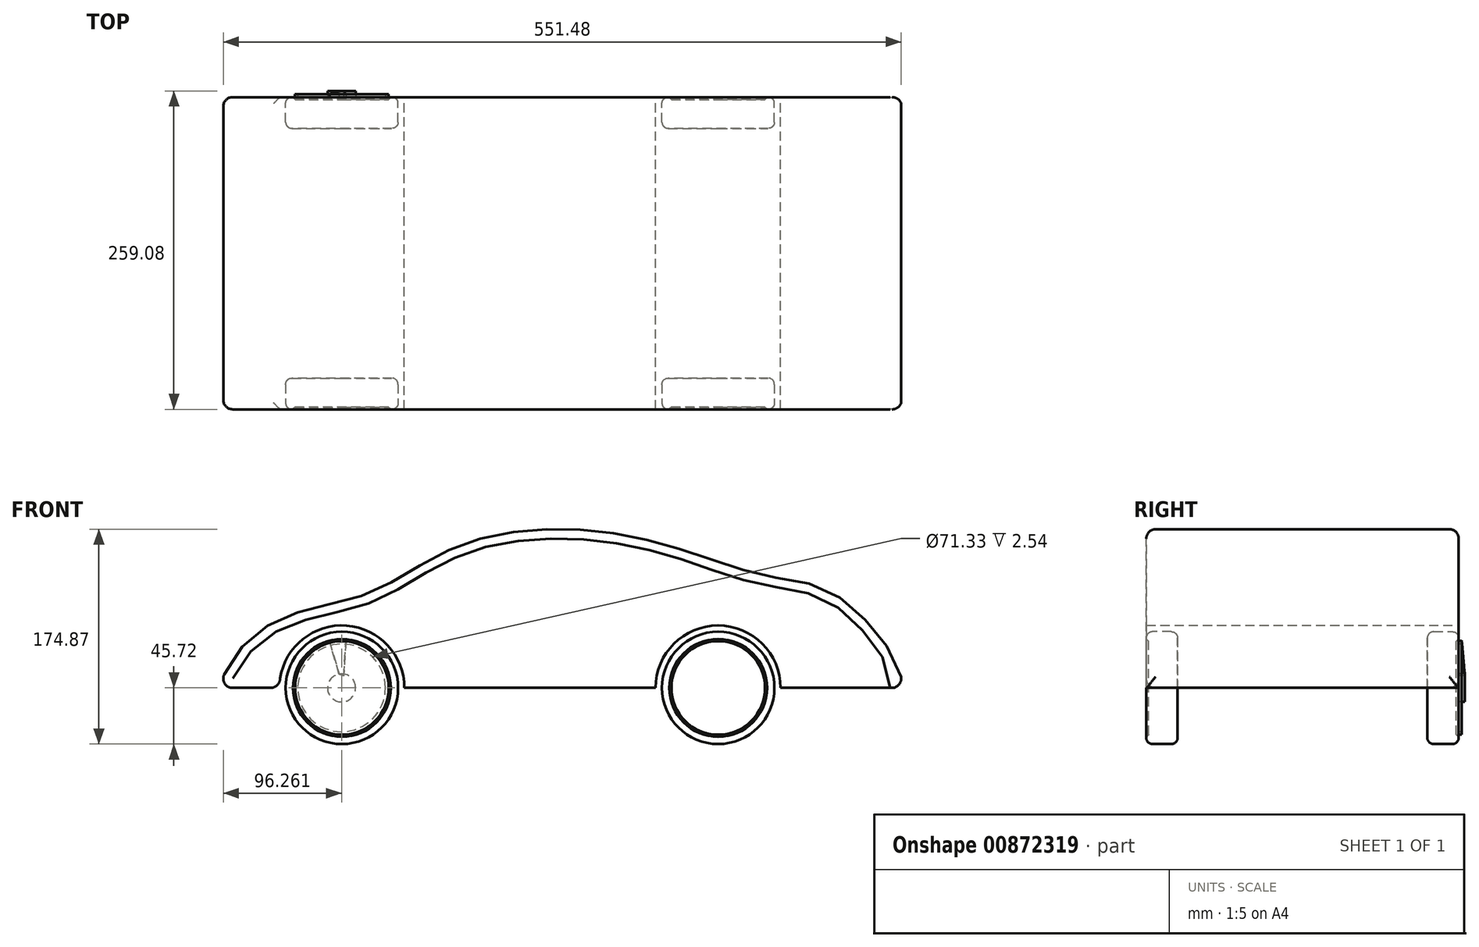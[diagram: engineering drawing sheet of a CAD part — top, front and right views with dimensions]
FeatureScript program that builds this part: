
annotation { "Feature Type Name" : "Feature", "Feature Type Description" : "" }
export const myFeature = defineFeature(function(context is Context, id is Id, definition is map)
    precondition{}
    {
        {
            var Q0;
            Q0=qCreatedBy(makeId("Front.planeOp"),FACE);
            var sketch = newSketch(context, id + "F0", { "sketchPlane" : qUnion([Q0])});
            skFitSpline(sketch, "E0", {"points": [v(0, 0) * mm, v(73.7, 64) * mm, v(127.71, 79.17) * mm, v(203.51, 118.59) * mm, v(340.8, 122.3) * mm, v(442.02, 91.83) * mm, v(507.62, 71.94) * mm, v(554.71, 0) * mm], "startDerivative": vector(332.9, 896.63) * mm, "endDerivative": vector(-140, -298.92) * mm});
            skLineSegment(sketch, "E1", {"start": v(0, 0) * mm, "end": v(49.58, 0) * mm});
            skCircle(sketch, "E2", {"center": v(100.38, 0) * mm, "radius": 50.8 * mm});
            skCircle(sketch, "E3", {"center": v(406.34, 0) * mm, "radius": 50.8 * mm});
            skLineSegment(sketch, "E4.trimOffspring", {"start": v(151.18, 0) * mm, "end": v(355.54, 0) * mm});
            skLineSegment(sketch, "E5.trimOffspring", {"start": v(457.14, 0) * mm, "end": v(554.71, 0) * mm});
            skPoint(sketch, "E6", {"position": v(253.36, 0) * mm});
            skSolve(sketch);
        }
        {
            var Q0;
            Q0=makeQuery(id+"F0.imprint","IMPRINT",FACE,{"disambiguationData":[TD([[makeQuery(id+"F0.imprint","IMPRINT",EDGE,{"derivedFrom":sQuery(id+"F0.wireOp",EDGE,"E0")}),-1.0]])]});
            extrude(context, id + "F1", {"entities" : qUnion([Q0]), "depth" : 254 * mm, "offsetDistance" : 25.4 * mm});
        }
        {
            var Q0;
            Q0=qCreatedBy(makeId("Front.planeOp"),FACE);
            var sketch = newSketch(context, id + "F2", { "sketchPlane" : qUnion([Q0])});
            skCircle(sketch, "E7", {"center": v(100.38, 0) * mm, "radius": 45.72 * mm});
            skSolve(sketch);
        }
        {
            var Q0;
            Q0 = qSketchRegion(id + "F2", true);
            extrude(context, id + "F3", {"entities" : qUnion([Q0]), "depth" : 25.4 * mm, "offsetDistance" : 25.4 * mm});
        }
        {
            var Q0;
            Q0=makeQuery(id+"F1.opExtrude","SWEPT_FACE",FACE,{"disambiguationData":[OSD([sQuery(id+"F0.wireOp",EDGE,"E1")])]});
            var Q1;
            Q1=makeQuery(id+"F1.opExtrude","SWEPT_FACE",FACE,{"disambiguationData":[OSD([sQuery(id+"F0.wireOp",EDGE,"E0")])]});
            fillet(context, id + "F4", {"entities" : qUnion([Q0, Q1]), "radius" : 7.62 * mm, "tangentPropagation" : true, "allowEdgeOverflow" : false});
        }
        {
            var Q0;
            Q0=makeQuery(id+"F3.opExtrude","CAP_FACE",FACE,{"disambiguationData":[OSD([sQuery(id+"F2.wireOp",EDGE,"E7")])],"isStart":true});
            var Q1;
            Q1=makeQuery(id+"F3.opExtrude","SWEPT_FACE",FACE,{"disambiguationData":[OSD([sQuery(id+"F2.wireOp",EDGE,"E7")])]});
            fillet(context, id + "F5", {"entities" : qUnion([Q0, Q1]), "radius" : 5.08 * mm, "tangentPropagation" : true, "allowEdgeOverflow" : false});
        }
        {
            var Q0;
            Q0=makeQuery(id+"F3.opExtrude","CAP_FACE",FACE,{"disambiguationData":[OSD([sQuery(id+"F2.wireOp",EDGE,"E7")])],"isStart":true});
            extrude(context, id + "F6", {"entities" : qUnion([Q0]), "operationType" : NewBodyOperationType.REMOVE, "oppositeDirection" : true, "depth" : 1.9 * mm, "offsetDistance" : 25.4 * mm, "hasDraft" : true, "draftAngle" : 3 * degree});
        }
        {
            var Q0;
            Q0=makeQuery(id+"F6.boolean.opBoolean","COPY",EDGE,{"derivedFrom":makeQuery(id+"F6.opExtrude","CAP_EDGE",EDGE,{"disambiguationData":[OSD([sQuery(id+"F2.wireOp",EDGE,"E7")])],"isStart":false})});
            chamfer(context, id + "F7", {"entities" : qUnion([Q0]), "width" : 2.54 * mm, "tangentPropagation" : true});
        }
        {
            var Q0;
            Q0=makeQuery(id+"F3.opExtrude","SWEPT_BODY",BODY,{"disambiguationData":[OSD([sQuery(id+"F2.wireOp",EDGE,"E7")])]});
            var Q1;
            Q1=qCreatedBy(makeId("Front.planeOp"),FACE);
            mirror(context, id + "F8", {"entities" : qUnion([Q0]), "mirrorPlane" : qUnion([Q1])});
        }
        {
            var Q0;
            Q0=makeQuery(id+"F8.opPattern","COPY",BODY,{"derivedFrom":makeQuery(id+"F3.opExtrude","SWEPT_BODY",BODY,{"disambiguationData":[OSD([sQuery(id+"F2.wireOp",EDGE,"E7")])]}),"instanceName":"1"});
            transform(context, id + "F9", {"entities" : qUnion([Q0]), "transformType" : TransformType.TRANSLATION_3D, "dx" : 0 * mm, "dy" : -254 * mm, "dz" : 0 * mm, "makeCopy" : false});
        }
        {
            var Q0;
            Q0=makeQuery(id+"F8.opPattern","COPY",BODY,{"derivedFrom":makeQuery(id+"F9.opPattern","COPY",BODY,{"derivedFrom":makeQuery(id+"F3.opExtrude","SWEPT_BODY",BODY,{"disambiguationData":[OSD([sQuery(id+"F2.wireOp",EDGE,"E7")])]}),"instanceName":"1"}),"instanceName":"1"});
            var Q1;
            Q1=makeQuery(id+"F3.opExtrude","SWEPT_BODY",BODY,{"disambiguationData":[OSD([sQuery(id+"F2.wireOp",EDGE,"E7")])]});
            var Q2;
            Q2=makeQuery(id+"F8.opPattern","COPY",BODY,{"derivedFrom":makeQuery(id+"F3.opExtrude","SWEPT_BODY",BODY,{"disambiguationData":[OSD([sQuery(id+"F2.wireOp",EDGE,"E7")])]}),"instanceName":"1"});
            transform(context, id + "F10", {"entities" : qUnion([Q0, Q1, Q2]), "transformType" : TransformType.TRANSLATION_3D, "dx" : 306.07 * mm, "dy" : 0 * mm, "dz" : 0 * mm, "makeCopy" : true});
        }
        {
            var Q0;
            Q0=makeQuery(id+"F2.imprint","IMPRINT",FACE,{"disambiguationData":[TD([[makeQuery(id+"F2.imprint","IMPRINT",EDGE,{"derivedFrom":sQuery(id+"F2.wireOp",EDGE,"E7")}),1.0]])]});
            var sketch = newSketch(context, id + "F11", { "sketchPlane" : qUnion([Q0])});
            skCircle(sketch, "E8", {"center": v(100.14, 0) * mm, "radius": 38.1 * mm});
            skCircle(sketch, "E9", {"center": v(100.14, 0) * mm, "radius": 35.66 * mm});
            skCircle(sketch, "E10", {"center": v(100.14, 0) * mm, "radius": 11.43 * mm});
            skSolve(sketch);
        }
        {
            var Q0;
            Q0=makeQuery(id+"F11.imprint","IMPRINT",FACE,{"disambiguationData":[TD([[makeQuery(id+"F11.imprint","IMPRINT",EDGE,{"derivedFrom":sQuery(id+"F11.wireOp",EDGE,"E10")}),1.0]])]});
            var Q1;
            Q1=makeQuery(id+"F11.imprint","IMPRINT",FACE,{"disambiguationData":[TD([[makeQuery(id+"F11.imprint","IMPRINT",EDGE,{"derivedFrom":sQuery(id+"F11.wireOp",EDGE,"E8")}),1.0]])]});
            extrude(context, id + "F12", {"entities" : qUnion([Q0, Q1]), "oppositeDirection" : true, "depth" : 2.54 * mm, "offsetDistance" : 25.4 * mm});
        }
        {
            var Q0;
            Q0=makeQuery(id+"F12.opExtrude","CAP_FACE",FACE,{"disambiguationData":[OSD([sQuery(id+"F11.wireOp",EDGE,"E10")])],"isStart":false});
            extrude(context, id + "F13", {"entities" : qUnion([Q0]), "operationType" : NewBodyOperationType.ADD, "depth" : 2.54 * mm, "offsetDistance" : 25.4 * mm});
        }
        {
            var Q0;
            Q0=makeQuery(id+"F12.opExtrude","CAP_FACE",FACE,{"disambiguationData":[OSD([sQuery(id+"F11.wireOp",EDGE,"E8"),sQuery(id+"F11.wireOp",EDGE,"E9")])],"isStart":false});
            var sketch = newSketch(context, id + "F14", { "sketchPlane" : qUnion([Q0])});
            skLineSegment(sketch, "E11", {"start": v(-138.24, 0) * mm, "end": v(0, 0) * mm, "construction": true});
            skLineSegment(sketch, "E12", {"start": v(-99.53, -38.1) * mm, "end": v(-99.53, 54.44) * mm, "construction": true});
            skPoint(sketch, "E13", {"position": v(-99.53, 9.67) * mm});
            skLineSegment(sketch, "E14", {"start": v(-101.9, 9.63) * mm, "end": v(-103.6, 37.64) * mm});
            skLineSegment(sketch, "E15", {"start": v(-95.99, 37.64) * mm, "end": v(-97.7, 9.63) * mm});
            skLineSegment(sketch, "E16", {"start": v(-103.6, 37.64) * mm, "end": v(-95.99, 37.64) * mm});
            skLineSegment(sketch, "E17", {"start": v(-101.9, 9.63) * mm, "end": v(-97.7, 9.63) * mm});
            skSolve(sketch);
        }
        {
            var Q0;
            {var subQ0=sQuery(id+"F14.wireOp",EDGE,"E17");Q0=makeQuery(id+"F14.imprint","IMPRINT",FACE,{"disambiguationData":[TD([[makeQuery(id+"F14.imprint","IMPRINT",EDGE,{"derivedFrom":subQ0}),1.0]])]});}
            var Q1;
            {var subQ0=sQuery(id+"F14.wireOp",EDGE,"E16");Q1=makeQuery(id+"F14.imprint","IMPRINT",FACE,{"disambiguationData":[TD([[makeQuery(id+"F14.imprint","IMPRINT",EDGE,{"derivedFrom":subQ0}),-1.0]])]});}
            var Q2;
            Q2=sQuery(id+"F14.wireOp",EDGE,"E17");
            var Q3;
            Q3=sQuery(id+"F14.wireOp",EDGE,"E15");
            var Q4;
            Q4=sQuery(id+"F14.wireOp",EDGE,"E16");
            var Q5;
            Q5=sQuery(id+"F14.wireOp",EDGE,"E14");
            extrude(context, id + "F15", {"entities" : qUnion([Q0, Q1]), "surfaceEntities" : qUnion([Q2, Q3, Q4, Q5]), "depth" : 5.08 * mm, "offsetDistance" : 25.4 * mm});
        }
        {
            var Q0;
            Q0=makeQuery(id+"F15.opExtrude","SWEPT_FACE",FACE,{"disambiguationData":[OSD([sQuery(id+"F14.wireOp",EDGE,"E14")])]});
            var sketch = newSketch(context, id + "F16", { "sketchPlane" : qUnion([Q0])});
            skLineSegment(sketch, "E18", {"start": v(5.08, 43.9) * mm, "end": v(7.62, 15.84) * mm});
            skLineSegment(sketch, "E19", {"start": v(7.62, 15.84) * mm, "end": v(2.54, 16.24) * mm});
            skLineSegment(sketch, "E20", {"start": v(2.54, 16.24) * mm, "end": v(2.54, 43.9) * mm});
            skLineSegment(sketch, "E21", {"start": v(2.54, 43.9) * mm, "end": v(5.08, 43.9) * mm});
            skSolve(sketch);
        }
        {
            var Q0;
            Q0=makeQuery(id+"F15.opExtrude","SWEPT_BODY",BODY,{"disambiguationData":[OSD([sQuery(id+"F14.wireOp",EDGE,"E14"),sQuery(id+"F14.wireOp",EDGE,"E15"),sQuery(id+"F14.wireOp",EDGE,"E16"),sQuery(id+"F14.wireOp",EDGE,"E17")])]});
            deleteBodies(context, id + "F17", {"entities" : qUnion([Q0])});
        }
        {
            var Q0;
            Q0=qCreatedBy(makeId("Top.planeOp"),FACE);
            var sketch = newSketch(context, id + "F18", { "sketchPlane" : qUnion([Q0])});
            skLineSegment(sketch, "E22", {"start": v(96.46, 0) * mm, "end": v(96.46, -56.7) * mm});
            skSolve(sketch);
        }
        {
            var Q0;
            Q0 = qSketchRegion(id + "F18", true);
            var Q1;
            Q1=makeQuery(id+"F16.imprint","IMPRINT",FACE,{"disambiguationData":[TD([[makeQuery(id+"F16.imprint","IMPRINT",EDGE,{"derivedFrom":sQuery(id+"F16.wireOp",EDGE,"E18")}),-1.0]])]});
            var Q2;
            Q2=sQuery(id+"F18.wireOp",EDGE,"E22");
            revolve(context, id + "F19", {"surfaceOperationType" : NewSurfaceOperationType.NEW, "entities" : qUnion([Q0, Q1]), "axis" : qUnion([Q2]), "revolveType" : RevolveType.ONE_DIRECTION, "angle" : 20 * degree});
        }
        {
            var Q0;
            Q0=makeQuery(id+"F19.opRevolve","SWEPT_BODY",BODY,{"disambiguationData":[OSD([sQuery(id+"F16.wireOp",EDGE,"E18"),sQuery(id+"F16.wireOp",EDGE,"E19"),sQuery(id+"F16.wireOp",EDGE,"E20"),sQuery(id+"F16.wireOp",EDGE,"E21")])]});
            transform(context, id + "F20", {"entities" : qUnion([Q0]), "transformType" : TransformType.TRANSLATION_3D, "dx" : 0 * mm, "dy" : -2.57 * mm, "dz" : 0 * mm, "makeCopy" : false});
        }
    });
